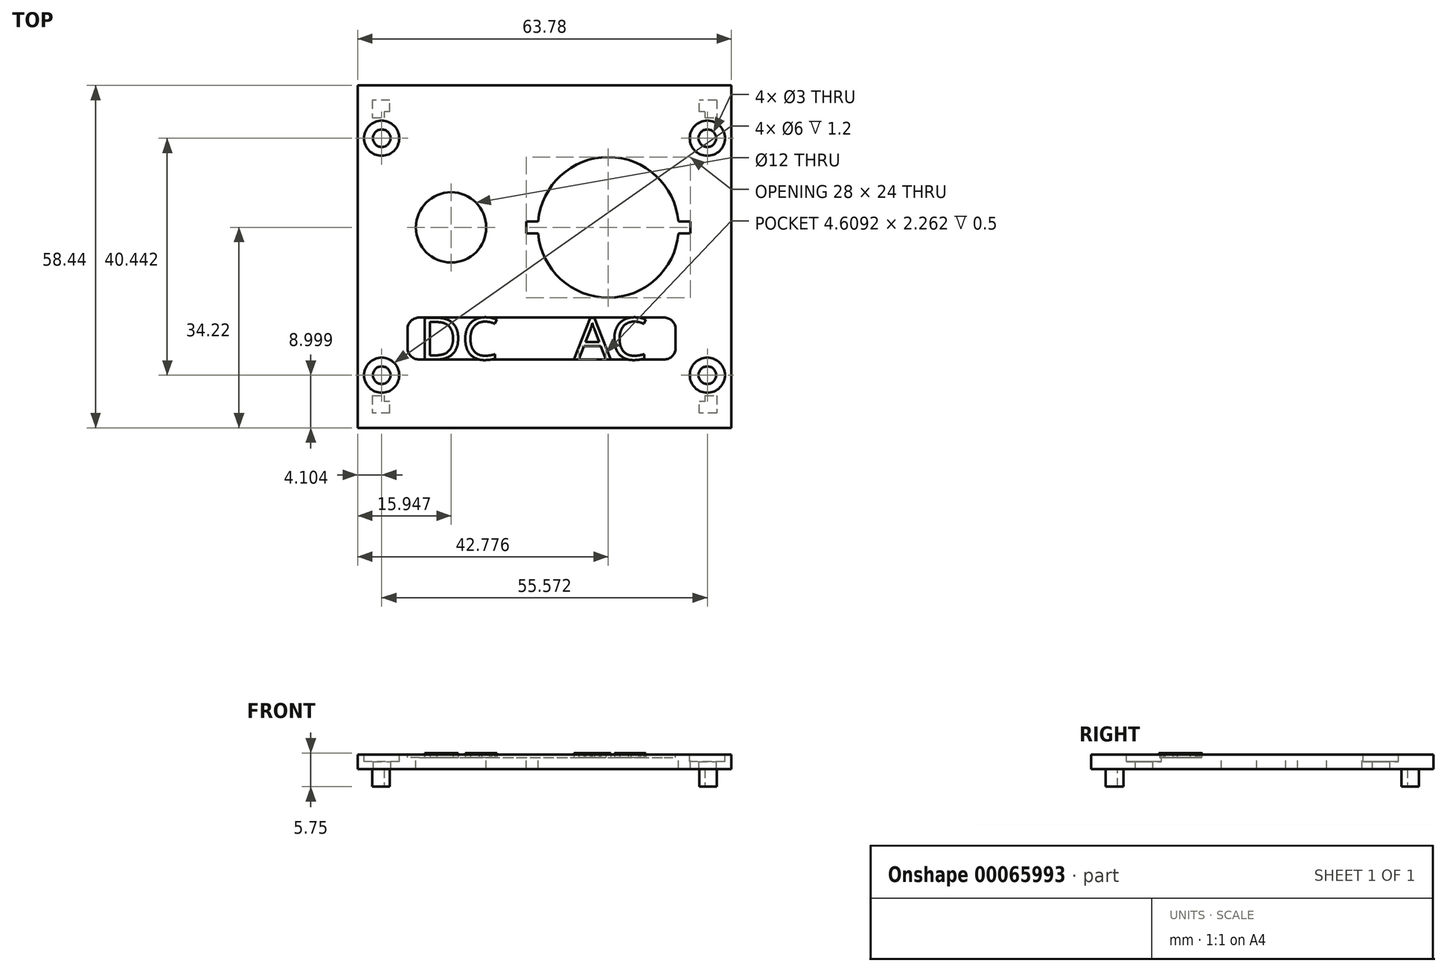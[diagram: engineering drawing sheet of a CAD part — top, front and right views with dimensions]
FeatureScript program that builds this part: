
annotation { "Feature Type Name" : "Feature", "Feature Type Description" : "" }
export const myFeature = defineFeature(function(context is Context, id is Id, definition is map)
    precondition{}
    {
        {
            var Q0;
            Q0=qCreatedBy(makeId("Top.planeOp"),FACE);
            var sketch = newSketch(context, id + "F0", { "sketchPlane" : qUnion([Q0])});
            skLineSegment(sketch, "E0.rect.bottom", {"start": v(31.89, -29.22) * mm, "end": v(-31.89, -29.22) * mm});
            skLineSegment(sketch, "E0.rect.top", {"start": v(31.89, 29.22) * mm, "end": v(-31.89, 29.22) * mm});
            skLineSegment(sketch, "E0.rect.left", {"start": v(31.89, -29.22) * mm, "end": v(31.89, 29.22) * mm});
            skLineSegment(sketch, "E0.rect.right", {"start": v(-31.89, -29.22) * mm, "end": v(-31.89, 29.22) * mm});
            skPoint(sketch, "E0.rect.middle", {"position": v(0, 0) * mm});
            skSolve(sketch);
        }
        {
            var Q0;
            Q0=makeQuery(id+"F0.imprint","IMPRINT",FACE,{"disambiguationData":[TD([[makeQuery(id+"F0.imprint","IMPRINT",EDGE,{"derivedFrom":sQuery(id+"F0.wireOp",EDGE,"E0.rect.bottom")}),-1.0]])]});
            extrude(context, id + "F1", {"entities" : qUnion([Q0]), "oppositeDirection" : true, "depth" : 2.5 * mm});
        }
        {
            var Q0;
            Q0=makeQuery(id+"F1.opExtrude","CAP_FACE",FACE,{"disambiguationData":[OSD([sQuery(id+"F0.wireOp",EDGE,"E0.rect.bottom"),sQuery(id+"F0.wireOp",EDGE,"E0.rect.top"),sQuery(id+"F0.wireOp",EDGE,"E0.rect.left"),sQuery(id+"F0.wireOp",EDGE,"E0.rect.right")])],"isStart":false});
            var sketch = newSketch(context, id + "F2", { "sketchPlane" : qUnion([Q0])});
            skLineSegment(sketch, "E1.rect.bottom", {"start": v(29.39, -26.72) * mm, "end": v(-29.39, -26.72) * mm});
            skLineSegment(sketch, "E1.rect.top", {"start": v(29.39, 26.72) * mm, "end": v(-29.39, 26.72) * mm});
            skLineSegment(sketch, "E1.rect.left", {"start": v(29.39, -26.72) * mm, "end": v(29.39, 26.72) * mm});
            skLineSegment(sketch, "E1.rect.right", {"start": v(-29.39, -26.72) * mm, "end": v(-29.39, 26.72) * mm});
            skPoint(sketch, "E1.rect.middle", {"position": v(0, 0) * mm});
            skLineSegment(sketch, "E2.rect.bottom", {"start": v(0, 0) * mm, "end": v(0, 0) * mm});
            skLineSegment(sketch, "E2.rect.top", {"start": v(0, 0) * mm, "end": v(0, 0) * mm});
            skLineSegment(sketch, "E2.rect.left", {"start": v(0, 0) * mm, "end": v(0, 0) * mm});
            skLineSegment(sketch, "E2.rect.right", {"start": v(0, 0) * mm, "end": v(0, 0) * mm});
            skLineSegment(sketch, "E3.rect.bottom", {"start": v(27.39, -24.72) * mm, "end": v(-27.39, -24.72) * mm});
            skLineSegment(sketch, "E3.rect.top", {"start": v(27.39, 24.72) * mm, "end": v(-27.39, 24.72) * mm});
            skLineSegment(sketch, "E3.rect.left", {"start": v(27.39, -24.72) * mm, "end": v(27.39, 24.72) * mm});
            skLineSegment(sketch, "E3.rect.right", {"start": v(-27.39, -24.72) * mm, "end": v(-27.39, 24.72) * mm});
            skSolve(sketch);
        }
        {
            var Q0;
            Q0=makeQuery(id+"F2.imprint","IMPRINT",FACE,{"disambiguationData":[TD([[makeQuery(id+"F2.imprint","IMPRINT",EDGE,{"derivedFrom":sQuery(id+"F2.wireOp",EDGE,"E1.rect.bottom")}),-1.0]])]});
            extrude(context, id + "F3", {"entities" : qUnion([Q0]), "operationType" : NewBodyOperationType.ADD, "depth" : 3 * mm});
        }
        {
            var Q0;
            Q0=makeQuery(id+"F3.opExtrude","CAP_FACE",FACE,{"disambiguationData":[OSD([sQuery(id+"F2.wireOp",EDGE,"E1.rect.bottom"),sQuery(id+"F2.wireOp",EDGE,"E1.rect.top"),sQuery(id+"F2.wireOp",EDGE,"E1.rect.left"),sQuery(id+"F2.wireOp",EDGE,"E1.rect.right"),sQuery(id+"F2.wireOp",EDGE,"E3.rect.bottom"),sQuery(id+"F2.wireOp",EDGE,"E3.rect.top"),sQuery(id+"F2.wireOp",EDGE,"E3.rect.left"),sQuery(id+"F2.wireOp",EDGE,"E3.rect.right")])],"isStart":false});
            var sketch = newSketch(context, id + "F4", { "sketchPlane" : qUnion([Q0])});
            skLineSegment(sketch, "E4.bottom", {"start": v(-26.39, 26.72) * mm, "end": v(26.39, 26.72) * mm});
            skLineSegment(sketch, "E4.top", {"start": v(-26.39, -26.72) * mm, "end": v(26.39, -26.72) * mm});
            skLineSegment(sketch, "E4.left", {"start": v(-26.39, 26.72) * mm, "end": v(-26.39, -26.72) * mm});
            skLineSegment(sketch, "E4.right", {"start": v(26.39, 26.72) * mm, "end": v(26.39, -26.72) * mm});
            skSolve(sketch);
        }
        {
            var Q0;
            {var subQ0=sQuery(id+"F4.wireOp",EDGE,"E4.bottom");Q0=makeQuery(id+"F4.imprint","IMPRINT",FACE,{"disambiguationData":[TD([[makeQuery(id+"F4.imprint","IMPRINT",EDGE,{"derivedFrom":subQ0}),1.0]])]});}
            var Q1;
            {var subQ0=sQuery(id+"F4.wireOp",EDGE,"E4.top");Q1=makeQuery(id+"F4.imprint","IMPRINT",FACE,{"disambiguationData":[TD([[makeQuery(id+"F4.imprint","IMPRINT",EDGE,{"derivedFrom":subQ0}),-1.0]])]});}
            extrude(context, id + "F5", {"entities" : qUnion([Q0, Q1]), "operationType" : NewBodyOperationType.REMOVE, "oppositeDirection" : true, "depth" : 3 * mm});
        }
        {
            var Q0;
            {var subQ0=sQuery(id+"F2.wireOp",EDGE,"E3.rect.bottom");var subQ1=sQuery(id+"F2.wireOp",EDGE,"E1.rect.right");var subQ2=sQuery(id+"F2.wireOp",EDGE,"E1.rect.top");var subQ3=sQuery(id+"F2.wireOp",EDGE,"E1.rect.bottom");var subQ4=sQuery(id+"F2.wireOp",EDGE,"E3.rect.top");var subQ6=sQuery(id+"F2.wireOp",EDGE,"E3.rect.right");Q0=makeQuery(id+"F5.boolean.opBoolean","SPLIT",FACE,{"disambiguationData":[TD([makeQuery(id+"F3.opExtrude","SWEPT_FACE",FACE,{"disambiguationData":[OSD([subQ1])]})])],"derivedFrom":makeQuery(id+"F3.opExtrude","CAP_FACE",FACE,{"disambiguationData":[OSD([subQ3,subQ2,sQuery(id+"F2.wireOp",EDGE,"E1.rect.left"),subQ1,subQ0,subQ4,sQuery(id+"F2.wireOp",EDGE,"E3.rect.left"),subQ6])],"isStart":false})});}
            var sketch = newSketch(context, id + "F6", { "sketchPlane" : qUnion([Q0])});
            skLineSegment(sketch, "E5.bottom", {"start": v(-29.39, 23.72) * mm, "end": v(29.39, 23.72) * mm});
            skLineSegment(sketch, "E5.top", {"start": v(-29.39, -23.72) * mm, "end": v(29.39, -23.72) * mm});
            skLineSegment(sketch, "E5.left", {"start": v(-29.39, 23.72) * mm, "end": v(-29.39, -23.72) * mm});
            skLineSegment(sketch, "E5.right", {"start": v(29.39, 23.72) * mm, "end": v(29.39, -23.72) * mm});
            skSolve(sketch);
        }
        {
            var Q0;
            {var subQ0=sQuery(id+"F6.wireOp",EDGE,"E5.right");Q0=makeQuery(id+"F6.imprint","IMPRINT",FACE,{"disambiguationData":[TD([[makeQuery(id+"F6.imprint","IMPRINT",EDGE,{"derivedFrom":subQ0}),-1.0]])]});}
            var Q1;
            {var subQ0=sQuery(id+"F6.wireOp",EDGE,"E5.left");Q1=makeQuery(id+"F6.imprint","IMPRINT",FACE,{"disambiguationData":[TD([[makeQuery(id+"F6.imprint","IMPRINT",EDGE,{"derivedFrom":subQ0}),-1.0]])]});}
            extrude(context, id + "F7", {"entities" : qUnion([Q0, Q1]), "operationType" : NewBodyOperationType.REMOVE, "oppositeDirection" : true, "depth" : 3 * mm});
        }
        {
            var Q0;
            Q0=makeQuery(id+"F1.opExtrude","CAP_FACE",FACE,{"disambiguationData":[OSD([sQuery(id+"F0.wireOp",EDGE,"E0.rect.bottom"),sQuery(id+"F0.wireOp",EDGE,"E0.rect.top"),sQuery(id+"F0.wireOp",EDGE,"E0.rect.left"),sQuery(id+"F0.wireOp",EDGE,"E0.rect.right")])],"isStart":true});
            var sketch = newSketch(context, id + "F8", { "sketchPlane" : qUnion([Q0])});
            skLineSegment(sketch, "E6", {"start": v(31.89, 5) * mm, "end": v(-31.89, 5) * mm, "construction": true});
            skCircle(sketch, "E7", {"center": v(-15.94, 5) * mm, "radius": 6 * mm});
            skCircle(sketch, "E8", {"center": v(10.89, 5) * mm, "radius": 12 * mm});
            skSolve(sketch);
        }
        {
            var Q0;
            Q0=makeQuery(id+"F8.imprint","IMPRINT",FACE,{"disambiguationData":[TD([[makeQuery(id+"F8.imprint","IMPRINT",EDGE,{"derivedFrom":sQuery(id+"F8.wireOp",EDGE,"E7")}),1.0]])]});
            var Q1;
            Q1=makeQuery(id+"F8.imprint","IMPRINT",FACE,{"disambiguationData":[TD([[makeQuery(id+"F8.imprint","IMPRINT",EDGE,{"derivedFrom":sQuery(id+"F8.wireOp",EDGE,"E8")}),1.0]])]});
            extrude(context, id + "F9", {"entities" : qUnion([Q0, Q1]), "operationType" : NewBodyOperationType.REMOVE, "oppositeDirection" : true, "depth" : 2.5 * mm});
        }
        {
            var Q0;
            Q0=qCreatedBy(makeId("Top.planeOp"),FACE);
            var sketch = newSketch(context, id + "F10", { "sketchPlane" : qUnion([Q0])});
            skLineSegment(sketch, "E9.bottom", {"start": v(-3.11, 6) * mm, "end": v(24.89, 6) * mm});
            skLineSegment(sketch, "E9.top", {"start": v(-3.11, 4) * mm, "end": v(24.89, 4) * mm});
            skLineSegment(sketch, "E9.left", {"start": v(-3.11, 6) * mm, "end": v(-3.11, 4) * mm});
            skLineSegment(sketch, "E9.right", {"start": v(24.89, 6) * mm, "end": v(24.89, 4) * mm});
            skSolve(sketch);
        }
        {
            var Q0;
            Q0=makeQuery(id+"F10.imprint","IMPRINT",FACE,{"disambiguationData":[TD([[makeQuery(id+"F10.imprint","IMPRINT",EDGE,{"derivedFrom":sQuery(id+"F10.wireOp",EDGE,"E9.bottom")}),-1.0]])]});
            extrude(context, id + "F11", {"entities" : qUnion([Q0]), "operationType" : NewBodyOperationType.REMOVE, "oppositeDirection" : true, "depth" : 3 * mm});
        }
        {
            var Q0;
            {var subQ0=sQuery(id+"F4.wireOp",EDGE,"E4.right");var subQ1=sQuery(id+"F4.wireOp",EDGE,"E4.left");var subQ2=sQuery(id+"F2.wireOp",EDGE,"E3.rect.bottom");var subQ3=sQuery(id+"F2.wireOp",EDGE,"E3.rect.top");var subQ4=sQuery(id+"F0.wireOp",EDGE,"E0.rect.right");var subQ5=sQuery(id+"F0.wireOp",EDGE,"E0.rect.left");var subQ6=sQuery(id+"F0.wireOp",EDGE,"E0.rect.top");var subQ7=sQuery(id+"F0.wireOp",EDGE,"E0.rect.bottom");var subQ8=makeQuery(id+"F1.opExtrude","CAP_FACE",FACE,{"disambiguationData":[OSD([subQ7,subQ6,subQ5,subQ4])],"isStart":false});Q0=makeQuery(id+"F7.boolean.opBoolean","MERGE",FACE,{"derivedFrom":[makeQuery(id+"F5.boolean.opBoolean","MERGE",FACE,{"derivedFrom":[makeQuery(id+"F3.boolean.opBoolean","SPLIT",FACE,{"disambiguationData":[TD([makeQuery(id+"F1.opExtrude","SWEPT_FACE",FACE,{"disambiguationData":[OSD([subQ7])]})])],"derivedFrom":subQ8}),makeQuery(id+"F3.boolean.opBoolean","SPLIT",FACE,{"disambiguationData":[TD([makeQuery(id+"F3.opExtrude","SWEPT_FACE",FACE,{"disambiguationData":[OSD([subQ2])]})])],"derivedFrom":subQ8}),makeQuery(id+"F5.opExtrude","CAP_FACE",FACE,{"disambiguationData":[OSD([subQ3,sQuery(id+"F4.wireOp",EDGE,"E4.bottom"),subQ1,subQ0])],"isStart":false}),makeQuery(id+"F5.opExtrude","CAP_FACE",FACE,{"disambiguationData":[OSD([subQ2,sQuery(id+"F4.wireOp",EDGE,"E4.top"),subQ1,subQ0])],"isStart":false})]}),makeQuery(id+"F7.opExtrude","CAP_FACE",FACE,{"disambiguationData":[OSD([sQuery(id+"F6.wireOp",EDGE,"E5.bottom"),sQuery(id+"F6.wireOp",EDGE,"E5.top"),sQuery(id+"F6.wireOp",EDGE,"E5.left"),sQuery(id+"F6.wireOp",EDGE,"E5.right")])],"isStart":false})]});}
            var sketch = newSketch(context, id + "F12", { "sketchPlane" : qUnion([Q0])});
            skLineSegment(sketch, "E10", {"start": v(-3.11, -6) * mm, "end": v(31.89, -6) * mm, "construction": true});
            skCircle(sketch, "E11", {"center": v(-27.79, -20.22) * mm, "radius": 1.5 * mm});
            skCircle(sketch, "E12", {"center": v(27.79, -20.22) * mm, "radius": 1.5 * mm});
            skCircle(sketch, "E13", {"center": v(-27.79, 20.22) * mm, "radius": 1.5 * mm});
            skCircle(sketch, "E14", {"center": v(27.79, 20.22) * mm, "radius": 1.5 * mm});
            skCircle(sketch, "E15", {"center": v(-27.79, -20.22) * mm, "radius": 3 * mm});
            skCircle(sketch, "E16", {"center": v(27.79, -20.22) * mm, "radius": 3 * mm});
            skCircle(sketch, "E17", {"center": v(27.79, 20.22) * mm, "radius": 3 * mm});
            skCircle(sketch, "E18", {"center": v(-27.79, 20.22) * mm, "radius": 3 * mm});
            skSolve(sketch);
        }
        {
            var Q0;
            Q0=makeQuery(id+"F12.imprint","IMPRINT",FACE,{"disambiguationData":[TD([[makeQuery(id+"F12.imprint","IMPRINT",EDGE,{"derivedFrom":sQuery(id+"F12.wireOp",EDGE,"E11")}),1.0]])]});
            var Q1;
            Q1=makeQuery(id+"F12.imprint","IMPRINT",FACE,{"disambiguationData":[TD([[makeQuery(id+"F12.imprint","IMPRINT",EDGE,{"derivedFrom":sQuery(id+"F12.wireOp",EDGE,"E12")}),1.0]])]});
            var Q2;
            Q2=makeQuery(id+"F12.imprint","IMPRINT",FACE,{"disambiguationData":[TD([[makeQuery(id+"F12.imprint","IMPRINT",EDGE,{"derivedFrom":sQuery(id+"F12.wireOp",EDGE,"E14")}),1.0]])]});
            var Q3;
            Q3=makeQuery(id+"F12.imprint","IMPRINT",FACE,{"disambiguationData":[TD([[makeQuery(id+"F12.imprint","IMPRINT",EDGE,{"derivedFrom":sQuery(id+"F12.wireOp",EDGE,"E13")}),1.0]])]});
            extrude(context, id + "F13", {"entities" : qUnion([Q0, Q1, Q2, Q3]), "operationType" : NewBodyOperationType.REMOVE, "oppositeDirection" : true, "depth" : 2.5 * mm});
        }
        {
            var Q0;
            Q0 = qSketchRegion(id + "F12", true);
            extrude(context, id + "F14", {"entities" : qUnion([Q0]), "operationType" : NewBodyOperationType.REMOVE, "depth" : 1.25 * mm});
        }
        {
            var Q0;
            Q0=makeQuery(id+"F1.opExtrude","CAP_FACE",FACE,{"disambiguationData":[OSD([sQuery(id+"F0.wireOp",EDGE,"E0.rect.bottom"),sQuery(id+"F0.wireOp",EDGE,"E0.rect.top"),sQuery(id+"F0.wireOp",EDGE,"E0.rect.left"),sQuery(id+"F0.wireOp",EDGE,"E0.rect.right")])],"isStart":true});
            var sketch = newSketch(context, id + "F15", { "sketchPlane" : qUnion([Q0])});
            skCircle(sketch, "E19", {"center": v(27.79, -20.22) * mm, "radius": 3 * mm});
            skCircle(sketch, "E20", {"center": v(-27.79, -20.22) * mm, "radius": 3 * mm});
            skCircle(sketch, "E21", {"center": v(-27.79, 20.22) * mm, "radius": 3 * mm});
            skCircle(sketch, "E22", {"center": v(27.79, 20.22) * mm, "radius": 3 * mm});
            skSolve(sketch);
        }
        {
            var Q0;
            Q0=makeQuery(id+"F15.imprint","IMPRINT",FACE,{"disambiguationData":[TD([[makeQuery(id+"F15.imprint","IMPRINT",EDGE,{"derivedFrom":sQuery(id+"F15.wireOp",EDGE,"E21")}),1.0]])]});
            var Q1;
            Q1=makeQuery(id+"F15.imprint","IMPRINT",FACE,{"disambiguationData":[TD([[makeQuery(id+"F15.imprint","IMPRINT",EDGE,{"derivedFrom":sQuery(id+"F15.wireOp",EDGE,"E22")}),1.0]])]});
            var Q2;
            Q2=makeQuery(id+"F15.imprint","IMPRINT",FACE,{"disambiguationData":[TD([[makeQuery(id+"F15.imprint","IMPRINT",EDGE,{"derivedFrom":sQuery(id+"F15.wireOp",EDGE,"E19")}),1.0]])]});
            var Q3;
            Q3=makeQuery(id+"F15.imprint","IMPRINT",FACE,{"disambiguationData":[TD([[makeQuery(id+"F15.imprint","IMPRINT",EDGE,{"derivedFrom":sQuery(id+"F15.wireOp",EDGE,"E20")}),1.0]])]});
            extrude(context, id + "F16", {"entities" : qUnion([Q0, Q1, Q2, Q3]), "operationType" : NewBodyOperationType.REMOVE, "oppositeDirection" : true, "depth" : 1.2 * mm});
        }
        {
            var Q0;
            Q0=makeQuery(id+"F1.opExtrude","CAP_FACE",FACE,{"disambiguationData":[OSD([sQuery(id+"F0.wireOp",EDGE,"E0.rect.bottom"),sQuery(id+"F0.wireOp",EDGE,"E0.rect.top"),sQuery(id+"F0.wireOp",EDGE,"E0.rect.left"),sQuery(id+"F0.wireOp",EDGE,"E0.rect.right")])],"isStart":true});
            var sketch = newSketch(context, id + "F17", { "sketchPlane" : qUnion([Q0])});
            skLineSegment(sketch, "E23.bottom", {"start": v(-21.39, -10.38) * mm, "end": v(20.39, -10.38) * mm});
            skLineSegment(sketch, "E23.top", {"start": v(-21.39, -17.55) * mm, "end": v(20.39, -17.55) * mm});
            skLineSegment(sketch, "E23.left", {"start": v(-23.39, -12.38) * mm, "end": v(-23.39, -15.55) * mm});
            skLineSegment(sketch, "E23.right", {"start": v(22.39, -12.38) * mm, "end": v(22.39, -15.55) * mm});
            skPoint(sketch, "E24.visualSharp", {"position": v(22.39, -10.38) * mm});
            skArc(sketch, "E24.filletArc", {"start": v(22.39, -12.38) * mm, "mid": v(21.8, -10.97) * mm, "end": v(20.39, -10.38) * mm});
            skPoint(sketch, "E25.visualSharp", {"position": v(22.39, -17.55) * mm});
            skArc(sketch, "E25.filletArc", {"start": v(20.39, -17.55) * mm, "mid": v(21.8, -16.97) * mm, "end": v(22.39, -15.55) * mm});
            skPoint(sketch, "E26.visualSharp", {"position": v(-23.39, -17.55) * mm});
            skArc(sketch, "E26.filletArc", {"start": v(-23.39, -15.55) * mm, "mid": v(-22.8, -16.97) * mm, "end": v(-21.39, -17.55) * mm});
            skPoint(sketch, "E27.visualSharp", {"position": v(-23.39, -10.38) * mm});
            skArc(sketch, "E27.filletArc", {"start": v(-21.39, -10.38) * mm, "mid": v(-22.8, -10.97) * mm, "end": v(-23.39, -12.38) * mm});
            skSolve(sketch);
        }
        {
            var Q0;
            Q0=makeQuery(id+"F17.imprint","IMPRINT",FACE,{"disambiguationData":[TD([[makeQuery(id+"F17.imprint","IMPRINT",EDGE,{"derivedFrom":sQuery(id+"F17.wireOp",EDGE,"E23.bottom")}),-1.0]])]});
            extrude(context, id + "F18", {"entities" : qUnion([Q0]), "operationType" : NewBodyOperationType.REMOVE, "oppositeDirection" : true, "depth" : .5 * mm});
        }
        {
            var Q0;
            Q0=makeQuery(id+"F18.boolean.opBoolean","COPY",FACE,{"derivedFrom":makeQuery(id+"F18.opExtrude","CAP_FACE",FACE,{"disambiguationData":[OSD([sQuery(id+"F17.wireOp",EDGE,"E23.bottom"),sQuery(id+"F17.wireOp",EDGE,"E23.top"),sQuery(id+"F17.wireOp",EDGE,"E23.left"),sQuery(id+"F17.wireOp",EDGE,"E23.right"),sQuery(id+"F17.wireOp",EDGE,"E24.filletArc"),sQuery(id+"F17.wireOp",EDGE,"E25.filletArc"),sQuery(id+"F17.wireOp",EDGE,"E26.filletArc"),sQuery(id+"F17.wireOp",EDGE,"E27.filletArc")])],"isStart":false})});
            var sketch = newSketch(context, id + "F19", { "sketchPlane" : qUnion([Q0])});
            skText(sketch, "E28", { "text": "DC", "fontName": "OpenSans-Regular.ttf"});
            skText(sketch, "E29", { "text": "AC", "fontName": "OpenSans-Regular.ttf"});
            const initialGuessF19  = {"E28": [-0.02139, -0.01755, 1, 0, 0.00717], "E29": [0.00501, -0.01755, 1, 0, 0.00717]};
            skSetInitialGuess(sketch, initialGuessF19);
            skSolve(sketch);
        }
        {
            var Q0;
            Q0 = qSketchRegion(id + "F19", true);
            extrude(context, id + "F20", {"entities" : qUnion([Q0]), "operationType" : NewBodyOperationType.ADD, "depth" : .75 * mm});
        }
    });
